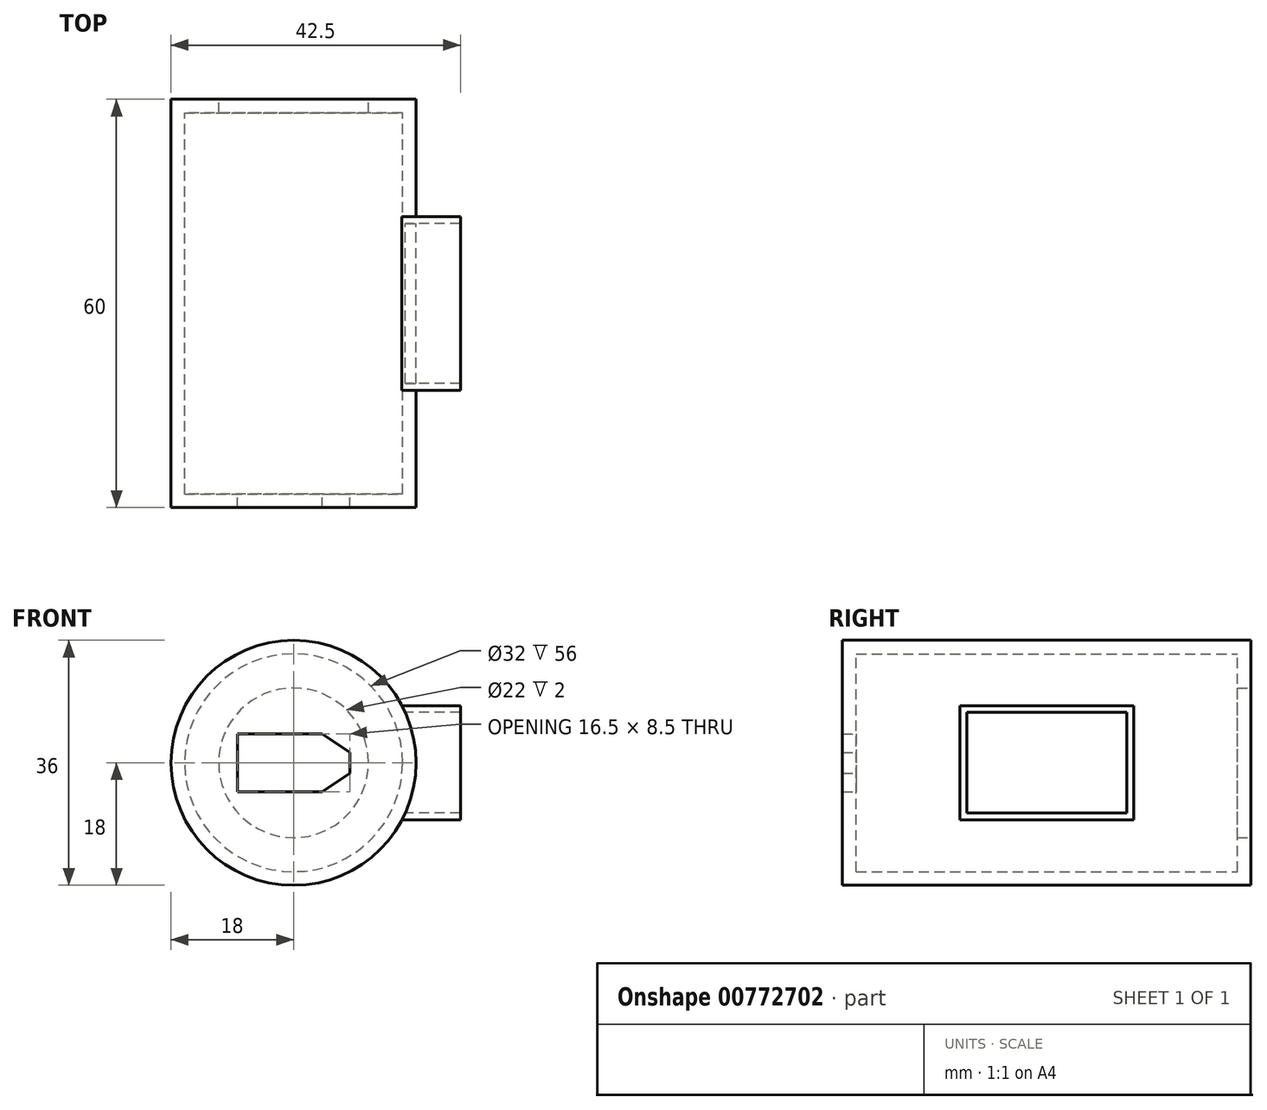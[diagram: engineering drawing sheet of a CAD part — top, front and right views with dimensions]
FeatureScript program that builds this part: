
annotation { "Feature Type Name" : "Feature", "Feature Type Description" : "" }
export const myFeature = defineFeature(function(context is Context, id is Id, definition is map)
    precondition{}
    {
        {
            var Q0;
            Q0=qCreatedBy(makeId("Front.planeOp"),FACE);
            var sketch = newSketch(context, id + "F0", { "sketchPlane" : qUnion([Q0])});
            skCircle(sketch, "E0", {"center": v(0, 0) * mm, "radius": 11 * mm});
            skCircle(sketch, "E1", {"center": v(0, 0) * mm, "radius": 18 * mm});
            skCircle(sketch, "E2", {"center": v(0, 0) * mm, "radius": 16 * mm});
            skLineSegment(sketch, "E3.bottom", {"start": v(8.25, 4.25) * mm, "end": v(-8.25, 4.25) * mm});
            skLineSegment(sketch, "E3.top", {"start": v(8.25, -4.25) * mm, "end": v(-8.25, -4.25) * mm});
            skLineSegment(sketch, "E3.left", {"start": v(8.25, 4.25) * mm, "end": v(8.25, -4.25) * mm});
            skLineSegment(sketch, "E3.right", {"start": v(-8.25, 4.25) * mm, "end": v(-8.25, -4.25) * mm});
            skLineSegment(sketch, "E4", {"start": v(-8.25, 4.25) * mm, "end": v(4.22, 4.25) * mm});
            skLineSegment(sketch, "E5", {"start": v(4.22, 4.25) * mm, "end": v(8.25, 1.5) * mm});
            skLineSegment(sketch, "E6", {"start": v(8.25, 1.5) * mm, "end": v(8.25, -1.5) * mm});
            skLineSegment(sketch, "E7", {"start": v(8.25, -1.5) * mm, "end": v(4.22, -4.25) * mm});
            skLineSegment(sketch, "E8", {"start": v(8.25, -4.25) * mm, "end": v(8.25, -1.5) * mm});
            skLineSegment(sketch, "E9", {"start": v(8.25, 1.5) * mm, "end": v(8.25, 4.25) * mm});
            skSolve(sketch);
        }
        {
            var Q0;
            Q0=makeQuery(id+"F0.imprint","IMPRINT",FACE,{"disambiguationData":[TD([[makeQuery(id+"F0.imprint","IMPRINT",EDGE,{"derivedFrom":sQuery(id+"F0.wireOp",EDGE,"E1")}),1.0]])]});
            extrude(context, id + "F1", {"entities" : qUnion([Q0]), "depth" : 60 * mm, "offsetDistance" : 25 * mm});
        }
        {
            var Q0;
            Q0=makeQuery(id+"F0.imprint","IMPRINT",FACE,{"disambiguationData":[TD([[makeQuery(id+"F0.imprint","IMPRINT",EDGE,{"derivedFrom":sQuery(id+"F0.wireOp",EDGE,"E0")}),-1.0]])]});
            extrude(context, id + "F2", {"entities" : qUnion([Q0]), "operationType" : NewBodyOperationType.ADD, "depth" : 8 * mm, "offsetDistance" : 25 * mm});
        }
        {
            var Q0;
            Q0=qCreatedBy(makeId("Right.planeOp"),FACE);
            var sketch = newSketch(context, id + "F3", { "sketchPlane" : qUnion([Q0])});
            skLineSegment(sketch, "E10.bottom", {"start": v(-41.75, 7.4) * mm, "end": v(-18.25, 7.4) * mm});
            skLineSegment(sketch, "E10.top", {"start": v(-41.75, -7.4) * mm, "end": v(-18.25, -7.4) * mm});
            skLineSegment(sketch, "E10.left", {"start": v(-41.75, 7.4) * mm, "end": v(-41.75, -7.4) * mm});
            skLineSegment(sketch, "E10.right", {"start": v(-18.25, 7.4) * mm, "end": v(-18.25, -7.4) * mm});
            skPoint(sketch, "E10.middle", {"position": v(-30, 0) * mm});
            skLineSegment(sketch, "E11.bottom", {"start": v(-42.75, 8.4) * mm, "end": v(-17.25, 8.4) * mm});
            skLineSegment(sketch, "E11.top", {"start": v(-42.75, -8.4) * mm, "end": v(-17.25, -8.4) * mm});
            skLineSegment(sketch, "E11.left", {"start": v(-42.75, 8.4) * mm, "end": v(-42.75, -8.4) * mm});
            skLineSegment(sketch, "E11.right", {"start": v(-17.25, 8.4) * mm, "end": v(-17.25, -8.4) * mm});
            skLineSegment(sketch, "E12.bottom", {"start": v(-18.25, 7.4) * mm, "end": v(-41.75, 7.4) * mm});
            skLineSegment(sketch, "E12.top", {"start": v(-18.25, -7.4) * mm, "end": v(-41.75, -7.4) * mm});
            skCircle(sketch, "E13", {"center": v(-37.6, 3.56) * mm, "radius": 3.16 * mm});
            skSolve(sketch);
        }
        {
            var Q0;
            Q0 = qSketchRegion(id + "F3", true);
            extrude(context, id + "F4", {"entities" : qUnion([Q0]), "operationType" : NewBodyOperationType.ADD, "depth" : 24.5 * mm, "offsetDistance" : 25 * mm});
        }
        {
            var Q0;
            {var subQ0=sQuery(id+"F3.wireOp",EDGE,"E11.left");Q0=makeQuery(id+"F4.boolean.opBoolean","SPLIT",FACE,{"disambiguationData":[TD([makeQuery(id+"F1.opExtrude","SWEPT_FACE",FACE,{"disambiguationData":[OSD([sQuery(id+"F0.wireOp",EDGE,"E2")])]})])],"derivedFrom":makeQuery(id+"F4.opExtrude","SWEPT_FACE",FACE,{"disambiguationData":[OSD([subQ0])]})});}
            extrude(context, id + "F5", {"entities" : qUnion([Q0]), "operationType" : NewBodyOperationType.REMOVE, "oppositeDirection" : true, "depth" : 28.5 * mm, "offsetDistance" : 25 * mm});
        }
        {
            var Q0;
            Q0=makeQuery(id+"F0.imprint","IMPRINT",FACE,{"disambiguationData":[TD([[makeQuery(id+"F0.imprint","IMPRINT",EDGE,{"derivedFrom":sQuery(id+"F0.wireOp",EDGE,"E3.bottom")}),1.0]])]});
            var Q1;
            {var subQ2=sQuery(id+"F0.wireOp",EDGE,"E7");Q1=makeQuery(id+"F0.imprint","IMPRINT",FACE,{"disambiguationData":[TD([[makeQuery(id+"F0.imprint","IMPRINT",EDGE,{"derivedFrom":subQ2}),1.0]])]});}
            var Q2;
            Q2=makeQuery(id+"F0.imprint","IMPRINT",FACE,{"disambiguationData":[TD([[makeQuery(id+"F0.imprint","IMPRINT",EDGE,{"derivedFrom":sQuery(id+"F0.wireOp",EDGE,"E0")}),1.0]])]});
            var Q3;
            Q3=makeQuery(id+"F0.imprint","IMPRINT",FACE,{"disambiguationData":[TD([[makeQuery(id+"F0.imprint","IMPRINT",EDGE,{"derivedFrom":sQuery(id+"F0.wireOp",EDGE,"E0")}),-1.0]])]});
            extrude(context, id + "F6", {"entities" : qUnion([Q0, Q1, Q2, Q3]), "operationType" : NewBodyOperationType.ADD, "depth" : 60 * mm, "offsetDistance" : 25 * mm});
        }
        {
            var Q0;
            Q0=makeQuery(id+"F0.imprint","IMPRINT",FACE,{"disambiguationData":[TD([[makeQuery(id+"F0.imprint","IMPRINT",EDGE,{"derivedFrom":sQuery(id+"F0.wireOp",EDGE,"E0")}),1.0]])]});
            var Q1;
            Q1=makeQuery(id+"F0.imprint","IMPRINT",FACE,{"disambiguationData":[TD([[makeQuery(id+"F0.imprint","IMPRINT",EDGE,{"derivedFrom":sQuery(id+"F0.wireOp",EDGE,"E3.bottom")}),1.0]])]});
            var Q2;
            {var subQ2=sQuery(id+"F0.wireOp",EDGE,"E7");Q2=makeQuery(id+"F0.imprint","IMPRINT",FACE,{"disambiguationData":[TD([[makeQuery(id+"F0.imprint","IMPRINT",EDGE,{"derivedFrom":subQ2}),1.0]])]});}
            var Q3;
            Q3=makeQuery(id+"F0.imprint","IMPRINT",FACE,{"disambiguationData":[TD([[makeQuery(id+"F0.imprint","IMPRINT",EDGE,{"derivedFrom":sQuery(id+"F0.wireOp",EDGE,"E0")}),-1.0]])]});
            extrude(context, id + "F7", {"entities" : qUnion([Q0, Q1, Q2, Q3]), "operationType" : NewBodyOperationType.REMOVE, "depth" : 58 * mm, "offsetDistance" : 25 * mm});
        }
        {
            var Q0;
            Q0=makeQuery(id+"F0.imprint","IMPRINT",FACE,{"disambiguationData":[TD([[makeQuery(id+"F0.imprint","IMPRINT",EDGE,{"derivedFrom":sQuery(id+"F0.wireOp",EDGE,"E0")}),-1.0]])]});
            extrude(context, id + "F8", {"entities" : qUnion([Q0]), "operationType" : NewBodyOperationType.ADD, "depth" : 2 * mm, "offsetDistance" : 25 * mm});
        }
    });
